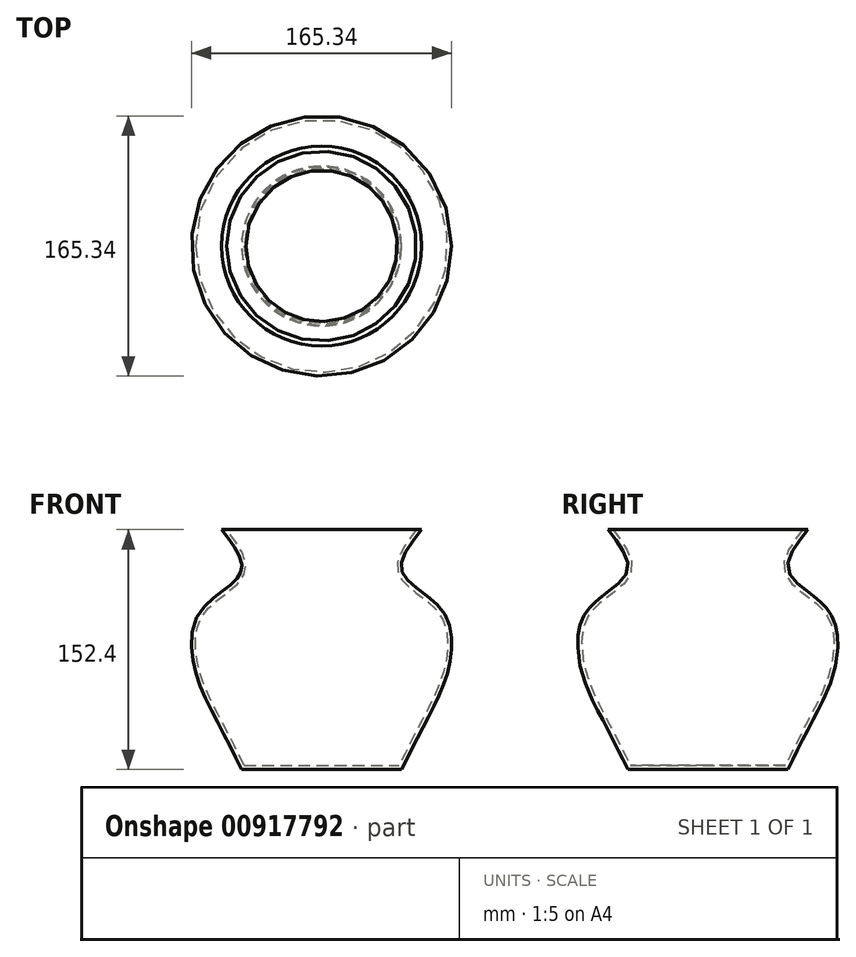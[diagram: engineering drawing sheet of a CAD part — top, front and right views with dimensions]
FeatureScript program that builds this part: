
annotation { "Feature Type Name" : "Feature", "Feature Type Description" : "" }
export const myFeature = defineFeature(function(context is Context, id is Id, definition is map)
    precondition{}
    {
        {
            var Q0;
            Q0=qCreatedBy(makeId("Top.planeOp"),FACE);
            var sketch = newSketch(context, id + "F0", { "sketchPlane" : qUnion([Q0])});
            skCircle(sketch, "E0", {"center": v(0, 0) * mm, "radius": 50.8 * mm});
            skSolve(sketch);
        }
        {
            var Q0;
            Q0=qCreatedBy(makeId("Top.planeOp"),FACE);
            cPlane(context, id + "F1", {"entities" : qUnion([Q0]), "cplaneType" : CPlaneType.OFFSET, "offset" : 25.4 * mm, "width" : 152.4 * mm, "height" : 152.4 * mm});
        }
        {
            var Q0;
            Q0=qCreatedBy(id+"F1.planeOp",FACE);
            var sketch = newSketch(context, id + "F2", { "sketchPlane" : qUnion([Q0])});
            skCircle(sketch, "E1", {"center": v(0, 0) * mm, "radius": 63.5 * mm});
            skSolve(sketch);
        }
        {
            var Q0;
            Q0=qCreatedBy(id+"F1.planeOp",FACE);
            cPlane(context, id + "F3", {"entities" : qUnion([Q0]), "cplaneType" : CPlaneType.OFFSET, "offset" : 25.4 * mm, "width" : 152.4 * mm, "height" : 152.4 * mm});
        }
        {
            var Q0;
            Q0=qCreatedBy(id+"F3.planeOp",FACE);
            var sketch = newSketch(context, id + "F4", { "sketchPlane" : qUnion([Q0])});
            skCircle(sketch, "E2", {"center": v(0, 0) * mm, "radius": 76.2 * mm});
            skSolve(sketch);
        }
        {
            var Q0;
            Q0=makeQuery(id+"F4.imprint","IMPRINT",FACE,{"disambiguationData":[TD([[makeQuery(id+"F4.imprint","IMPRINT",EDGE,{"derivedFrom":sQuery(id+"F4.wireOp",EDGE,"E2")}),1.0]])]});
            cPlane(context, id + "F5", {"entities" : qUnion([Q0]), "cplaneType" : CPlaneType.OFFSET, "offset" : 25.4 * mm, "width" : 152.4 * mm, "height" : 152.4 * mm});
        }
        {
            var Q0;
            Q0=qCreatedBy(id+"F5.planeOp",FACE);
            var sketch = newSketch(context, id + "F6", { "sketchPlane" : qUnion([Q0])});
            skCircle(sketch, "E3", {"center": v(0, 0) * mm, "radius": 82.55 * mm});
            skSolve(sketch);
        }
        {
            var Q0;
            Q0=qCreatedBy(id+"F5.planeOp",FACE);
            cPlane(context, id + "F7", {"entities" : qUnion([Q0]), "cplaneType" : CPlaneType.OFFSET, "offset" : 25.4 * mm, "width" : 152.4 * mm, "height" : 152.4 * mm});
        }
        {
            var Q0;
            Q0=qCreatedBy(id+"F7.planeOp",FACE);
            var sketch = newSketch(context, id + "F8", { "sketchPlane" : qUnion([Q0])});
            skCircle(sketch, "E4", {"center": v(0, 0) * mm, "radius": 76.2 * mm});
            skSolve(sketch);
        }
        {
            var Q0;
            Q0=qCreatedBy(id+"F7.planeOp",FACE);
            cPlane(context, id + "F9", {"entities" : qUnion([Q0]), "cplaneType" : CPlaneType.OFFSET, "offset" : 25.4 * mm, "width" : 152.4 * mm, "height" : 152.4 * mm});
        }
        {
            var Q0;
            Q0=qCreatedBy(id+"F9.planeOp",FACE);
            var sketch = newSketch(context, id + "F10", { "sketchPlane" : qUnion([Q0])});
            skCircle(sketch, "E5", {"center": v(0, 0) * mm, "radius": 50.8 * mm});
            skSolve(sketch);
        }
        {
            var Q0;
            Q0=qCreatedBy(id+"F9.planeOp",FACE);
            cPlane(context, id + "F11", {"entities" : qUnion([Q0]), "cplaneType" : CPlaneType.OFFSET, "offset" : 25.4 * mm, "width" : 152.4 * mm, "height" : 152.4 * mm});
        }
        {
            var Q0;
            Q0=qCreatedBy(id+"F11.planeOp",FACE);
            var sketch = newSketch(context, id + "F12", { "sketchPlane" : qUnion([Q0])});
            skCircle(sketch, "E6", {"center": v(0, 0) * mm, "radius": 63.5 * mm});
            skSolve(sketch);
        }
        {
            var Q0;
            Q0=makeQuery(id+"F0.imprint","IMPRINT",FACE,{"disambiguationData":[TD([[makeQuery(id+"F0.imprint","IMPRINT",EDGE,{"derivedFrom":sQuery(id+"F0.wireOp",EDGE,"E0")}),1.0]])]});
            var Q1;
            Q1=makeQuery(id+"F2.imprint","IMPRINT",FACE,{"disambiguationData":[TD([[makeQuery(id+"F2.imprint","IMPRINT",EDGE,{"derivedFrom":sQuery(id+"F2.wireOp",EDGE,"E1")}),1.0]])]});
            var Q2;
            Q2=makeQuery(id+"F4.imprint","IMPRINT",FACE,{"disambiguationData":[TD([[makeQuery(id+"F4.imprint","IMPRINT",EDGE,{"derivedFrom":sQuery(id+"F4.wireOp",EDGE,"E2")}),1.0]])]});
            var Q3;
            Q3=makeQuery(id+"F6.imprint","IMPRINT",FACE,{"disambiguationData":[TD([[makeQuery(id+"F6.imprint","IMPRINT",EDGE,{"derivedFrom":sQuery(id+"F6.wireOp",EDGE,"E3")}),1.0]])]});
            var Q4;
            Q4=makeQuery(id+"F8.imprint","IMPRINT",FACE,{"disambiguationData":[TD([[makeQuery(id+"F8.imprint","IMPRINT",EDGE,{"derivedFrom":sQuery(id+"F8.wireOp",EDGE,"E4")}),1.0]])]});
            var Q5;
            Q5=makeQuery(id+"F10.imprint","IMPRINT",FACE,{"disambiguationData":[TD([[makeQuery(id+"F10.imprint","IMPRINT",EDGE,{"derivedFrom":sQuery(id+"F10.wireOp",EDGE,"E5")}),1.0]])]});
            var Q6;
            Q6=makeQuery(id+"F12.imprint","IMPRINT",FACE,{"disambiguationData":[TD([[makeQuery(id+"F12.imprint","IMPRINT",EDGE,{"derivedFrom":sQuery(id+"F12.wireOp",EDGE,"E6")}),1.0]])]});
            loft(context, id + "F13", {"sheetProfilesArray" : [{ "sheetProfileEntities" : qUnion([Q0]) }, { "sheetProfileEntities" : qUnion([Q1]) }, { "sheetProfileEntities" : qUnion([Q2]) }, { "sheetProfileEntities" : qUnion([Q3]) }, { "sheetProfileEntities" : qUnion([Q4]) }, { "sheetProfileEntities" : qUnion([Q5]) }, { "sheetProfileEntities" : qUnion([Q6]) }]});
        }
        {
            var Q0;
            Q0=makeQuery(id+"F13.opLoft","CAP_FACE",FACE,{"disambiguationData":[OSD([makeQuery(id+"F12.imprint","IMPRINT",FACE,{"disambiguationData":[TD([[makeQuery(id+"F12.imprint","IMPRINT",EDGE,{"derivedFrom":sQuery(id+"F12.wireOp",EDGE,"E6")}),1.0]])]})])],"isStart":true});
            shell(context, id + "F14", {"entities" : qUnion([Q0]), "thickness" : 2.54 * mm});
        }
    });
